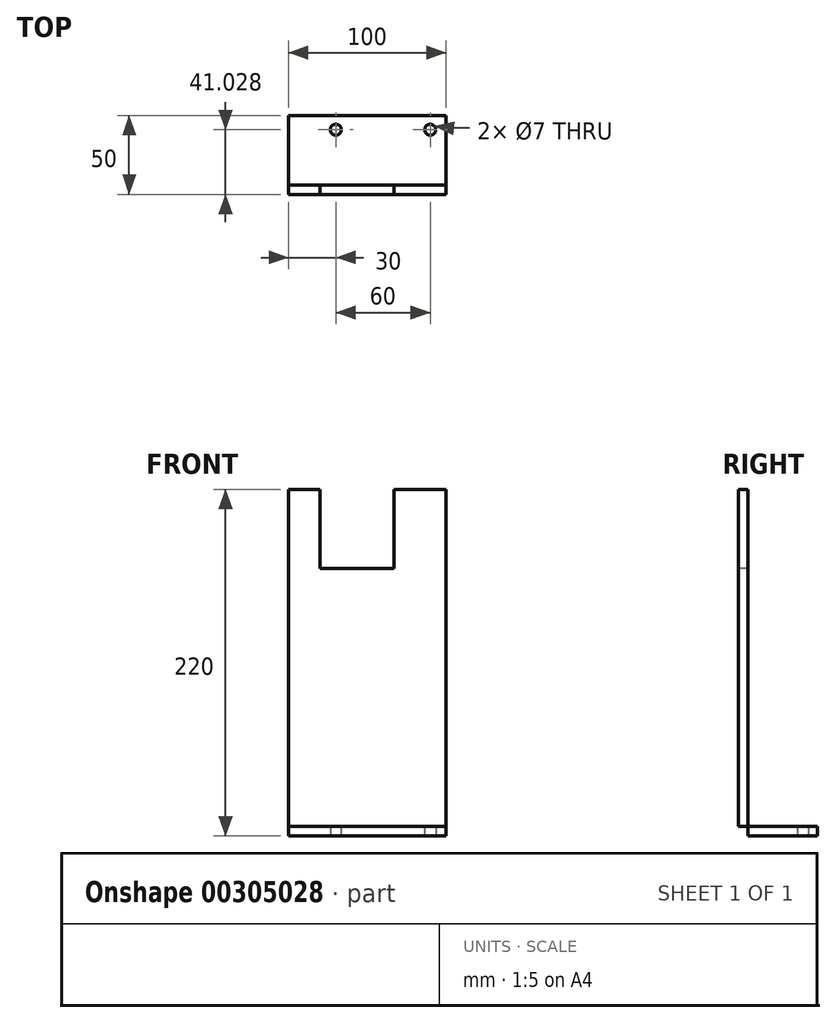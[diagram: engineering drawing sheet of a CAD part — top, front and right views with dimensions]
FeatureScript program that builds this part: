
annotation { "Feature Type Name" : "Feature", "Feature Type Description" : "" }
export const myFeature = defineFeature(function(context is Context, id is Id, definition is map)
    precondition{}
    {
        {
            var Q0;
            Q0=qCreatedBy(makeId("Right.planeOp"),FACE);
            var sketch = newSketch(context, id + "F0", { "sketchPlane" : qUnion([Q0])});
            skLineSegment(sketch, "E0.bottom", {"start": v(0, 0) * mm, "end": v(-6, 0) * mm});
            skLineSegment(sketch, "E0.top", {"start": v(0, 220) * mm, "end": v(-6, 220) * mm});
            skLineSegment(sketch, "E0.left", {"start": v(0, 0) * mm, "end": v(0, 220) * mm});
            skLineSegment(sketch, "E0.right", {"start": v(-6, 0) * mm, "end": v(-6, 220) * mm});
            skLineSegment(sketch, "E1.bottom", {"start": v(0, 0) * mm, "end": v(-50, 0) * mm});
            skLineSegment(sketch, "E1.top", {"start": v(0, 6) * mm, "end": v(-50, 6) * mm});
            skLineSegment(sketch, "E1.left", {"start": v(0, 0) * mm, "end": v(0, 6) * mm});
            skLineSegment(sketch, "E1.right", {"start": v(-50, 0) * mm, "end": v(-50, 6) * mm});
            skSolve(sketch);
        }
        {
            var Q0;
            {var subQ0=sQuery(id+"F0.wireOp",EDGE,"E0.top");Q0=makeQuery(id+"F0.imprint","IMPRINT",FACE,{"disambiguationData":[TD([[makeQuery(id+"F0.imprint","IMPRINT",EDGE,{"derivedFrom":subQ0}),1.0]])]});}
            var Q1;
            {var subQ5=sQuery(id+"F0.wireOp",EDGE,"E1.left");Q1=makeQuery(id+"F0.imprint","IMPRINT",FACE,{"disambiguationData":[TD([[makeQuery(id+"F0.imprint","IMPRINT",EDGE,{"derivedFrom":subQ5}),1.0]])]});}
            var Q2;
            {var subQ5=sQuery(id+"F0.wireOp",EDGE,"E1.right");Q2=makeQuery(id+"F0.imprint","IMPRINT",FACE,{"disambiguationData":[TD([[makeQuery(id+"F0.imprint","IMPRINT",EDGE,{"derivedFrom":subQ5}),-1.0]])]});}
            extrude(context, id + "F1", {"entities" : qUnion([Q0, Q1, Q2]), "depth" : 100 * mm});
        }
        {
            var Q0;
            Q0=qCreatedBy(makeId("Top.planeOp"),FACE);
            var sketch = newSketch(context, id + "F2", { "sketchPlane" : qUnion([Q0])});
            skLineSegment(sketch, "E2", {"start": v(30, 0) * mm, "end": v(30, -50.46) * mm, "construction": true});
            skLineSegment(sketch, "E3", {"start": v(90, 0) * mm, "end": v(90, -50.33) * mm, "construction": true});
            skLineSegment(sketch, "E4", {"start": v(0, -41.03) * mm, "end": v(100, -41.03) * mm, "construction": true});
            skCircle(sketch, "E5", {"center": v(30, -41.03) * mm, "radius": 3.5 * mm});
            skCircle(sketch, "E6", {"center": v(90, -41.03) * mm, "radius": 3.5 * mm});
            skSolve(sketch);
        }
        {
            var Q0;
            Q0=sQuery(id+"F2.wireOp",VERTEX,"E5.center");
            var Q1;
            Q1=sQuery(id+"F2.wireOp",VERTEX,"E6.center");
            var Q2;
            Q2=makeQuery(id+"F1.opExtrude","SWEPT_BODY",BODY,{"disambiguationData":[OSD([sQuery(id+"F0.wireOp",EDGE,"E0.top"),sQuery(id+"F0.wireOp",EDGE,"E0.left"),sQuery(id+"F0.wireOp",EDGE,"E0.right"),sQuery(id+"F0.wireOp",EDGE,"E1.bottom"),sQuery(id+"F0.wireOp",EDGE,"E1.top"),sQuery(id+"F0.wireOp",EDGE,"E1.left"),sQuery(id+"F0.wireOp",EDGE,"E1.right")])]});
            hole(context, id + "F3", {"style" : HoleStyle.SIMPLE, "endStyle" : HoleEndStyle.THROUGH, "oppositeDirection" : true, "holeDiameter" : 7 * mm, "tappedDepth" : 12 * mm, "tapClearance" : 3, "locations" : qUnion([Q0, Q1]), "scope" : qUnion([Q2])});
        }
        {
            var Q0;
            Q0=qCreatedBy(makeId("Front.planeOp"),FACE);
            var sketch = newSketch(context, id + "F4", { "sketchPlane" : qUnion([Q0])});
            skLineSegment(sketch, "E7", {"start": v(20, 220) * mm, "end": v(20, 170) * mm});
            skLineSegment(sketch, "E8", {"start": v(20, 170) * mm, "end": v(67, 170) * mm});
            skLineSegment(sketch, "E9", {"start": v(67, 170) * mm, "end": v(67, 220) * mm});
            skLineSegment(sketch, "E10", {"start": v(67, 220) * mm, "end": v(20, 220) * mm});
            skSolve(sketch);
        }
        {
            var Q0;
            Q0=makeQuery(id+"F4.imprint","IMPRINT",FACE,{"disambiguationData":[TD([[makeQuery(id+"F4.imprint","IMPRINT",EDGE,{"derivedFrom":sQuery(id+"F4.wireOp",EDGE,"E7")}),1.0]])]});
            extrude(context, id + "F5", {"entities" : qUnion([Q0]), "operationType" : NewBodyOperationType.REMOVE, "depth" : 25 * mm});
        }
        {
            var Q0;
            Q0=makeQuery(id+"F1.opExtrude","SWEPT_BODY",BODY,{"disambiguationData":[OSD([sQuery(id+"F0.wireOp",EDGE,"E0.top"),sQuery(id+"F0.wireOp",EDGE,"E0.left"),sQuery(id+"F0.wireOp",EDGE,"E0.right"),sQuery(id+"F0.wireOp",EDGE,"E1.bottom"),sQuery(id+"F0.wireOp",EDGE,"E1.top"),sQuery(id+"F0.wireOp",EDGE,"E1.left"),sQuery(id+"F0.wireOp",EDGE,"E1.right")])]});
            var Q1;
            Q1=qCreatedBy(makeId("Front.planeOp"),FACE);
            mirror(context, id + "F6", {"entities" : qUnion([Q0]), "mirrorPlane" : qUnion([Q1])});
        }
        {
            var Q0;
            Q0=makeQuery(id+"F6.opPattern","COPY",BODY,{"derivedFrom":makeQuery(id+"F1.opExtrude","SWEPT_BODY",BODY,{"disambiguationData":[OSD([sQuery(id+"F0.wireOp",EDGE,"E0.top"),sQuery(id+"F0.wireOp",EDGE,"E0.left"),sQuery(id+"F0.wireOp",EDGE,"E0.right"),sQuery(id+"F0.wireOp",EDGE,"E1.bottom"),sQuery(id+"F0.wireOp",EDGE,"E1.top"),sQuery(id+"F0.wireOp",EDGE,"E1.left"),sQuery(id+"F0.wireOp",EDGE,"E1.right")])]}),"instanceName":"1"});
            deleteBodies(context, id + "F7", {"entities" : qUnion([Q0])});
        }
        {
            var Q0;
            Q0=makeQuery(id+"F1.opExtrude","SWEPT_BODY",BODY,{"disambiguationData":[OSD([sQuery(id+"F0.wireOp",EDGE,"E0.top"),sQuery(id+"F0.wireOp",EDGE,"E0.left"),sQuery(id+"F0.wireOp",EDGE,"E0.right"),sQuery(id+"F0.wireOp",EDGE,"E1.bottom"),sQuery(id+"F0.wireOp",EDGE,"E1.top"),sQuery(id+"F0.wireOp",EDGE,"E1.left"),sQuery(id+"F0.wireOp",EDGE,"E1.right")])]});
            var Q1;
            Q1=qCreatedBy(makeId("Front.planeOp"),FACE);
            mirror(context, id + "F8", {"entities" : qUnion([Q0]), "mirrorPlane" : qUnion([Q1])});
        }
        {
            var Q0;
            Q0=makeQuery(id+"F1.opExtrude","SWEPT_BODY",BODY,{"disambiguationData":[OSD([sQuery(id+"F0.wireOp",EDGE,"E0.top"),sQuery(id+"F0.wireOp",EDGE,"E0.left"),sQuery(id+"F0.wireOp",EDGE,"E0.right"),sQuery(id+"F0.wireOp",EDGE,"E1.bottom"),sQuery(id+"F0.wireOp",EDGE,"E1.top"),sQuery(id+"F0.wireOp",EDGE,"E1.left"),sQuery(id+"F0.wireOp",EDGE,"E1.right")])]});
            deleteBodies(context, id + "F9", {"entities" : qUnion([Q0])});
        }
    });
